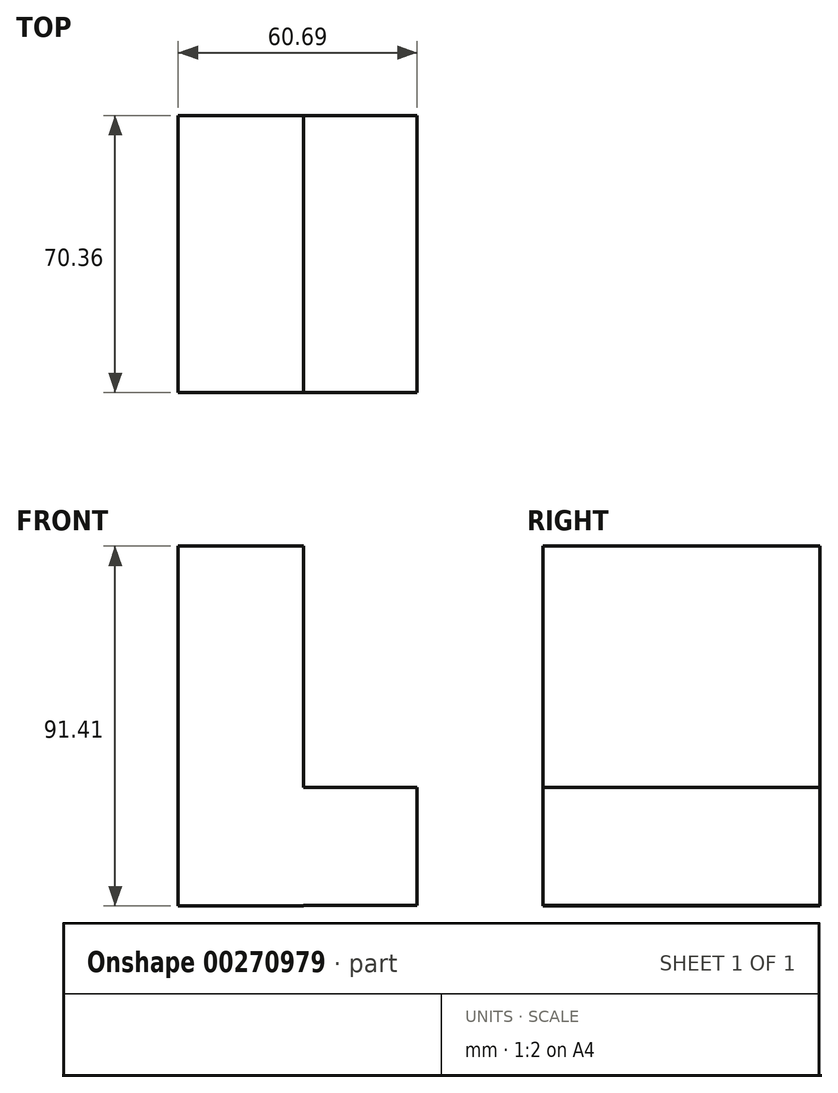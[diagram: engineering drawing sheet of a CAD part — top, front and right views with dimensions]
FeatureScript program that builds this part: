
annotation { "Feature Type Name" : "Feature", "Feature Type Description" : "" }
export const myFeature = defineFeature(function(context is Context, id is Id, definition is map)
    precondition{}
    {
        {
            var Q0;
            Q0=qCreatedBy(makeId("Front.planeOp"),FACE);
            var sketch = newSketch(context, id + "F0", { "sketchPlane" : qUnion([Q0])});
            skLineSegment(sketch, "E0.bottom", {"start": v(-50.7, 42.88) * mm, "end": v(-18.85, 42.88) * mm});
            skLineSegment(sketch, "E0.top", {"start": v(-50.7, -48.53) * mm, "end": v(-18.85, -48.53) * mm});
            skLineSegment(sketch, "E0.left", {"start": v(-50.7, 42.88) * mm, "end": v(-50.7, -48.53) * mm});
            skLineSegment(sketch, "E0.right", {"start": v(-18.85, 42.88) * mm, "end": v(-18.85, -48.53) * mm});
            skLineSegment(sketch, "E1.bottom", {"start": v(-18.85, -18.38) * mm, "end": v(9.99, -18.38) * mm});
            skLineSegment(sketch, "E1.top", {"start": v(-18.85, -48.35) * mm, "end": v(9.99, -48.35) * mm});
            skLineSegment(sketch, "E1.left", {"start": v(-18.85, -18.38) * mm, "end": v(-18.85, -48.35) * mm});
            skLineSegment(sketch, "E1.right", {"start": v(9.99, -18.38) * mm, "end": v(9.99, -48.35) * mm});
            skSolve(sketch);
        }
        {
            var Q0;
            Q0 = qSketchRegion(id + "F0", true);
            extrude(context, id + "F1", {"entities" : qUnion([Q0]), "depth" : 70.36 * mm});
        }
    });
